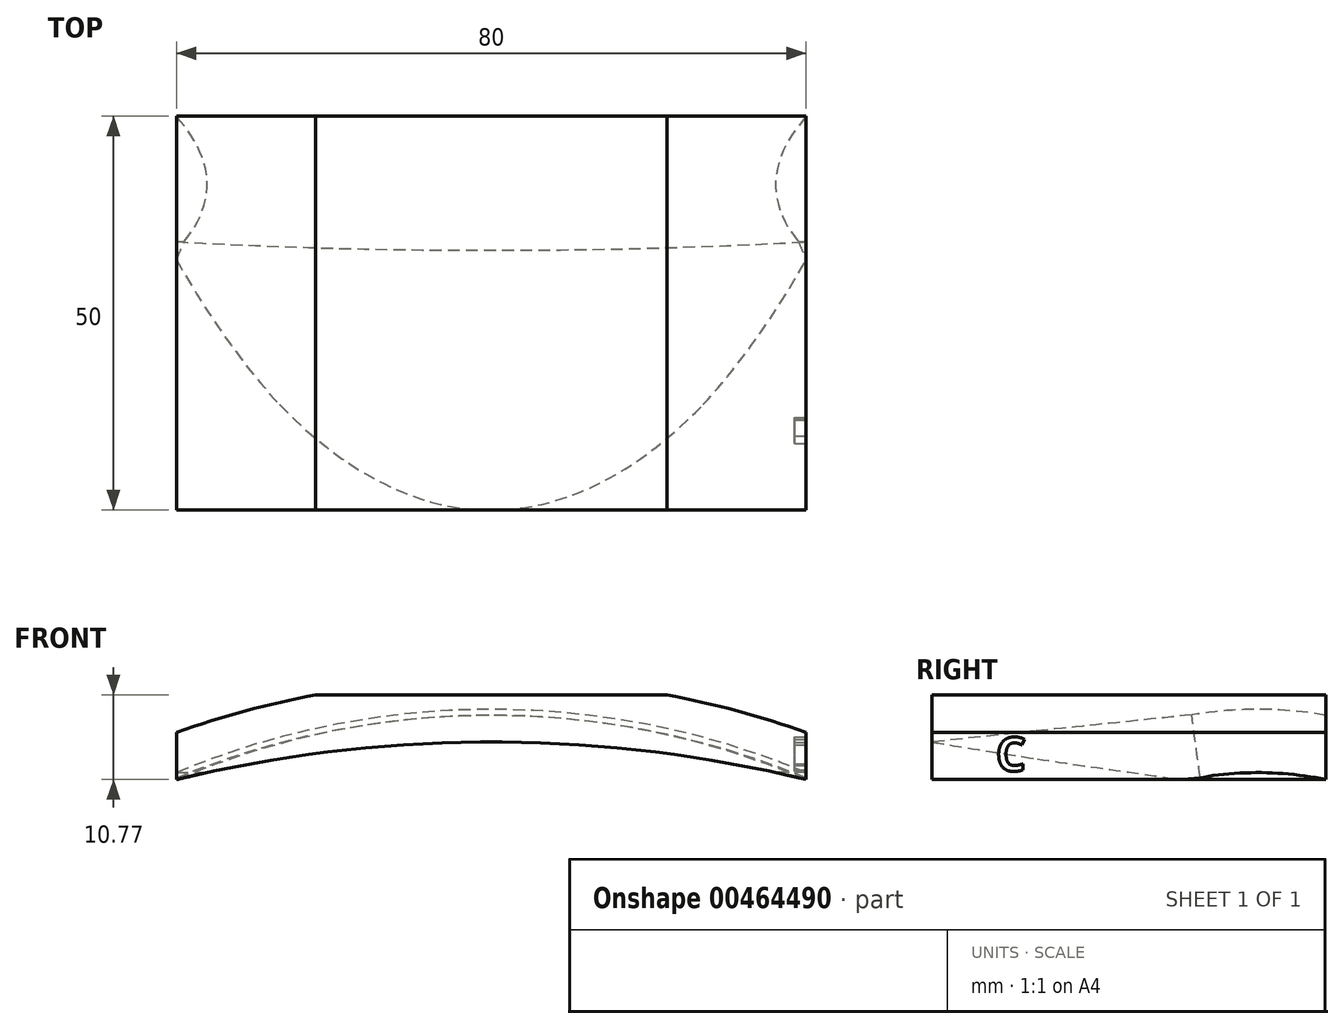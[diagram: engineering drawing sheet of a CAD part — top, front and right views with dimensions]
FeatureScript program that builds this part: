
annotation { "Feature Type Name" : "Feature", "Feature Type Description" : "" }
export const myFeature = defineFeature(function(context is Context, id is Id, definition is map)
    precondition{}
    {
        {
            var Q0;
            Q0=qCreatedBy(makeId("Front.planeOp"),FACE);
            var sketch = newSketch(context, id + "F0", { "sketchPlane" : qUnion([Q0])});
            skArc(sketch, "E0", {"start": v(80, 0) * mm, "mid": v(40, 4.77) * mm, "end": v(0, 0) * mm});
            skLineSegment(sketch, "E1", {"start": v(0, 0) * mm, "end": v(0, 6) * mm});
            skLineSegment(sketch, "E2", {"start": v(17.7, 10.77) * mm, "end": v(62.3, 10.77) * mm});
            skLineSegment(sketch, "E3", {"start": v(80, 6) * mm, "end": v(80, 0) * mm});
            skArc(sketch, "E4", {"start": v(80, 6) * mm, "mid": v(71.24, 8.72) * mm, "end": v(62.3, 10.77) * mm});
            skPoint(sketch, "E5.orphan", {"position": v(80, 10.77) * mm});
            skArc(sketch, "E6.trimOffspring", {"start": v(17.7, 10.77) * mm, "mid": v(8.76, 8.72) * mm, "end": v(0, 6) * mm});
            skSolve(sketch);
        }
        {
            var Q0;
            Q0=qSketchRegion(id+"F0",true);
            extrude(context, id + "F1", {"entities" : qUnion([Q0]), "depth" : 25 * mm, "hasSecondDirection" : true, "secondDirectionOppositeDirection" : true, "secondDirectionDepth" : 25 * mm});
        }
        {
            var Q0;
            Q0=qCreatedBy(makeId("Right.planeOp"),FACE);
            cPlane(context, id + "F2", {"entities" : qUnion([Q0]), "cplaneType" : CPlaneType.OFFSET, "offset" : 35 * mm, "width" : 150 * mm, "height" : 150 * mm});
        }
        {
            var Q0;
            Q0=qCreatedBy(id+"F2.planeOp",FACE);
            var sketch = newSketch(context, id + "F3", { "sketchPlane" : qUnion([Q0])});
            skLineSegment(sketch, "E7", {"start": v(-29.46, 6) * mm, "end": v(30.4, 6) * mm, "construction": true});
            skLineSegment(sketch, "E8", {"start": v(25, 10.7) * mm, "end": v(25, 0) * mm, "construction": true});
            skArc(sketch, "E9", {"start": v(25, 8) * mm, "mid": v(16.5, 8.75) * mm, "end": v(8, 8.05) * mm});
            skPoint(sketch, "E9.endSnap0", {"position": v(0.47, 6) * mm});
            skLineSegment(sketch, "E10", {"start": v(8, 8.05) * mm, "end": v(-12, 6) * mm});
            skPoint(sketch, "E11.orphan", {"position": v(0, 6) * mm});
            skLineSegment(sketch, "E12", {"start": v(-12, 6) * mm, "end": v(-40, 3) * mm});
            skSolve(sketch);
        }
        {
            var Q0;
            Q0=makeQuery(id+"F1.opExtrude","CAP_FACE",FACE,{"disambiguationData":[OSD([sQuery(id+"F0.wireOp",EDGE,"E0"),sQuery(id+"F0.wireOp",EDGE,"E1"),sQuery(id+"F0.wireOp",EDGE,"E2"),sQuery(id+"F0.wireOp",EDGE,"E3"),sQuery(id+"F0.wireOp",EDGE,"E4"),sQuery(id+"F0.wireOp",EDGE,"E6.trimOffspring")])],"isStart":true});
            var sketch = newSketch(context, id + "F4", { "sketchPlane" : qUnion([Q0])});
            skArc(sketch, "E13", {"start": v(0, 0) * mm, "mid": v(-40, 8.17) * mm, "end": v(-80, 0) * mm});
            skLineSegment(sketch, "E14", {"start": v(-80, 0) * mm, "end": v(0, 0) * mm});
            skSolve(sketch);
        }
        {
            var Q0;
            Q0=makeQuery(id+"F4.imprint","IMPRINT",FACE,{"disambiguationData":[TD([[makeQuery(id+"F4.imprint","IMPRINT",EDGE,{"derivedFrom":sQuery(id+"F4.wireOp",EDGE,"E14")}),1.0]])]});
            var Q1;
            Q1=makeQuery(id+"F4.imprint","IMPRINT",FACE,{"disambiguationData":[TD([[makeQuery(id+"F4.imprint","IMPRINT",EDGE,{"derivedFrom":sQuery(id+"F4.wireOp",EDGE,"E13")}),1.0]])]});
            var Q2;
            Q2=sQuery(id+"F3.wireOp",EDGE,"E9");
            var Q3;
            Q3=sQuery(id+"F3.wireOp",EDGE,"E10");
            var Q4;
            Q4=sQuery(id+"F3.wireOp",EDGE,"E12");
            sweep(context, id + "F5", {"operationType" : NewBodyOperationType.REMOVE, "profiles" : qUnion([Q0, Q1]), "path" : qUnion([Q2, Q3, Q4])});
        }
        {
            var Q0;
            {var subQ1=sQuery(id+"F0.wireOp",EDGE,"E4");var subQ2=sQuery(id+"F0.wireOp",EDGE,"E3");Q0=makeQuery(id+"F5.boolean.opBoolean","SPLIT",FACE,{"disambiguationData":[TD([makeQuery(id+"F1.opExtrude","SWEPT_FACE",FACE,{"disambiguationData":[OSD([subQ1])]})])],"derivedFrom":makeQuery(id+"F1.opExtrude","SWEPT_FACE",FACE,{"disambiguationData":[OSD([subQ2])]})});}
            var sketch = newSketch(context, id + "F6", { "sketchPlane" : qUnion([Q0])});
            skText(sketch, "E15", { "text": "C", "fontName": "OpenSans-Bold.ttf"});
            const initialGuessF6  = {"E15": [-0.0169, 0.00109, 1, 0, 0.00432]};
            skSetInitialGuess(sketch, initialGuessF6);
            skSolve(sketch);
        }
        {
            var Q0;
            Q0 = qSketchRegion(id + "F6", true);
            extrude(context, id + "F7", {"entities" : qUnion([Q0]), "operationType" : NewBodyOperationType.REMOVE, "oppositeDirection" : true, "depth" : 1.5 * mm, "offsetDistance" : 25 * mm});
        }
    });
